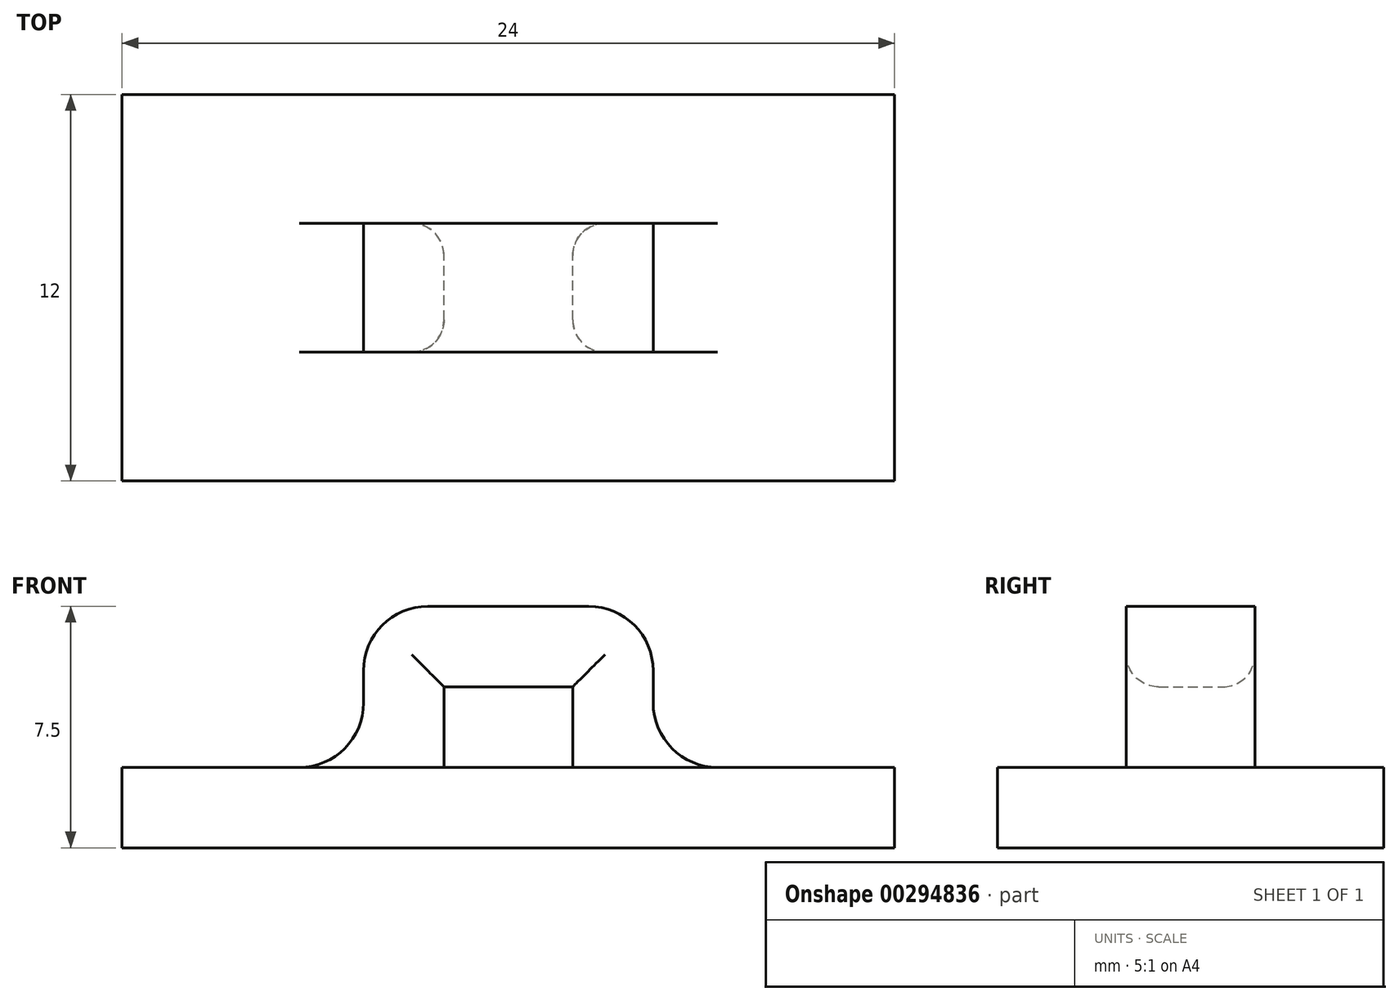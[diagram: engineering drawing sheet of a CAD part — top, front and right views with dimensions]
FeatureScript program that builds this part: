
annotation { "Feature Type Name" : "Feature", "Feature Type Description" : "" }
export const myFeature = defineFeature(function(context is Context, id is Id, definition is map)
    precondition{}
    {
        {
            var Q0;
            Q0=qCreatedBy(makeId("Top.planeOp"),FACE);
            var sketch = newSketch(context, id + "F0", { "sketchPlane" : qUnion([Q0])});
            skLineSegment(sketch, "E0.bottom", {"start": v(-12, 6) * mm, "end": v(12, 6) * mm});
            skLineSegment(sketch, "E0.top", {"start": v(-12, -6) * mm, "end": v(12, -6) * mm});
            skLineSegment(sketch, "E0.left", {"start": v(-12, 6) * mm, "end": v(-12, -6) * mm});
            skLineSegment(sketch, "E0.right", {"start": v(12, 6) * mm, "end": v(12, -6) * mm});
            skSolve(sketch);
        }
        {
            var Q0;
            Q0 = qSketchRegion(id + "F0", true);
            extrude(context, id + "F1", {"entities" : qUnion([Q0]), "depth" : 2.5 * mm});
        }
        {
            var Q0;
            Q0=qCreatedBy(makeId("Front.planeOp"),FACE);
            var sketch = newSketch(context, id + "F2", { "sketchPlane" : qUnion([Q0])});
            skLineSegment(sketch, "E1.bottom", {"start": v(-4.5, 7.5) * mm, "end": v(4.5, 7.5) * mm});
            skLineSegment(sketch, "E1.top", {"start": v(-4.5, 2.03) * mm, "end": v(-2, 2.03) * mm});
            skLineSegment(sketch, "E1.left", {"start": v(-4.5, 7.5) * mm, "end": v(-4.5, 2.03) * mm});
            skLineSegment(sketch, "E1.right", {"start": v(4.5, 7.5) * mm, "end": v(4.5, 2.03) * mm});
            skLineSegment(sketch, "E2.bottom", {"start": v(-2, 5) * mm, "end": v(2, 5) * mm});
            skLineSegment(sketch, "E2.left", {"start": v(-2, 5) * mm, "end": v(-2, 2.03) * mm});
            skLineSegment(sketch, "E2.right", {"start": v(2, 5) * mm, "end": v(2, 2.03) * mm});
            skLineSegment(sketch, "E3.trimOffspring", {"start": v(2, 2.03) * mm, "end": v(4.5, 2.03) * mm});
            skSolve(sketch);
        }
        {
            var Q0;
            Q0 = qSketchRegion(id + "F2", true);
            extrude(context, id + "F3", {"entities" : qUnion([Q0]), "operationType" : NewBodyOperationType.ADD, "endBound" : BoundingType.SYMMETRIC, "depth" : 4 * mm});
        }
        {
            var Q0;
            Q0=makeQuery(id+"F3.opExtrude","SWEPT_EDGE",EDGE,{"disambiguationData":[OSD([sQuery(id+"F2.wireOp",EDGE,"E1.bottom"),sQuery(id+"F2.wireOp",EDGE,"E1.right")])]});
            var Q1;
            Q1=makeQuery(id+"F3.opExtrude","SWEPT_EDGE",EDGE,{"disambiguationData":[OSD([sQuery(id+"F2.wireOp",EDGE,"E1.bottom"),sQuery(id+"F2.wireOp",EDGE,"E1.left")])]});
            var Q2;
            Q2=makeQuery(id+"F3.boolean.opBoolean","INTERSECT",EDGE,{"derivedFrom":[makeQuery(id+"F1.opExtrude","CAP_FACE",FACE,{"disambiguationData":[OSD([sQuery(id+"F0.wireOp",EDGE,"E0.bottom"),sQuery(id+"F0.wireOp",EDGE,"E0.top"),sQuery(id+"F0.wireOp",EDGE,"E0.left"),sQuery(id+"F0.wireOp",EDGE,"E0.right")])],"isStart":false}),makeQuery(id+"F3.opExtrude","SWEPT_FACE",FACE,{"disambiguationData":[OSD([sQuery(id+"F2.wireOp",EDGE,"E1.right")])]})]});
            var Q3;
            Q3=makeQuery(id+"F3.boolean.opBoolean","INTERSECT",EDGE,{"derivedFrom":[makeQuery(id+"F1.opExtrude","CAP_FACE",FACE,{"disambiguationData":[OSD([sQuery(id+"F0.wireOp",EDGE,"E0.bottom"),sQuery(id+"F0.wireOp",EDGE,"E0.top"),sQuery(id+"F0.wireOp",EDGE,"E0.left"),sQuery(id+"F0.wireOp",EDGE,"E0.right")])],"isStart":false}),makeQuery(id+"F3.opExtrude","SWEPT_FACE",FACE,{"disambiguationData":[OSD([sQuery(id+"F2.wireOp",EDGE,"E1.left")])]})]});
            fillet(context, id + "F4", {"entities" : qUnion([Q0, Q1, Q2, Q3]), "radius" : 2 * mm, "tangentPropagation" : true, "allowEdgeOverflow" : false});
        }
        {
            var Q0;
            Q0=makeQuery(id+"F3.opExtrude","CAP_EDGE",EDGE,{"disambiguationData":[OSD([sQuery(id+"F2.wireOp",EDGE,"E2.bottom")])],"isStart":false});
            var Q1;
            Q1=makeQuery(id+"F3.opExtrude","CAP_EDGE",EDGE,{"disambiguationData":[OSD([sQuery(id+"F2.wireOp",EDGE,"E2.bottom")])],"isStart":true});
            var Q2;
            Q2=makeQuery(id+"F3.opExtrude","CAP_EDGE",EDGE,{"disambiguationData":[OSD([sQuery(id+"F2.wireOp",EDGE,"E2.right")])],"isStart":true});
            var Q3;
            Q3=makeQuery(id+"F3.opExtrude","CAP_EDGE",EDGE,{"disambiguationData":[OSD([sQuery(id+"F2.wireOp",EDGE,"E2.left")])],"isStart":true});
            var Q4;
            Q4=makeQuery(id+"F3.opExtrude","CAP_EDGE",EDGE,{"disambiguationData":[OSD([sQuery(id+"F2.wireOp",EDGE,"E2.right")])],"isStart":false});
            var Q5;
            Q5=makeQuery(id+"F3.opExtrude","CAP_EDGE",EDGE,{"disambiguationData":[OSD([sQuery(id+"F2.wireOp",EDGE,"E2.left")])],"isStart":false});
            fillet(context, id + "F5", {"entities" : qUnion([Q0, Q1, Q2, Q3, Q4, Q5]), "radius" : 1 * mm, "tangentPropagation" : true, "allowEdgeOverflow" : false});
        }
    });
